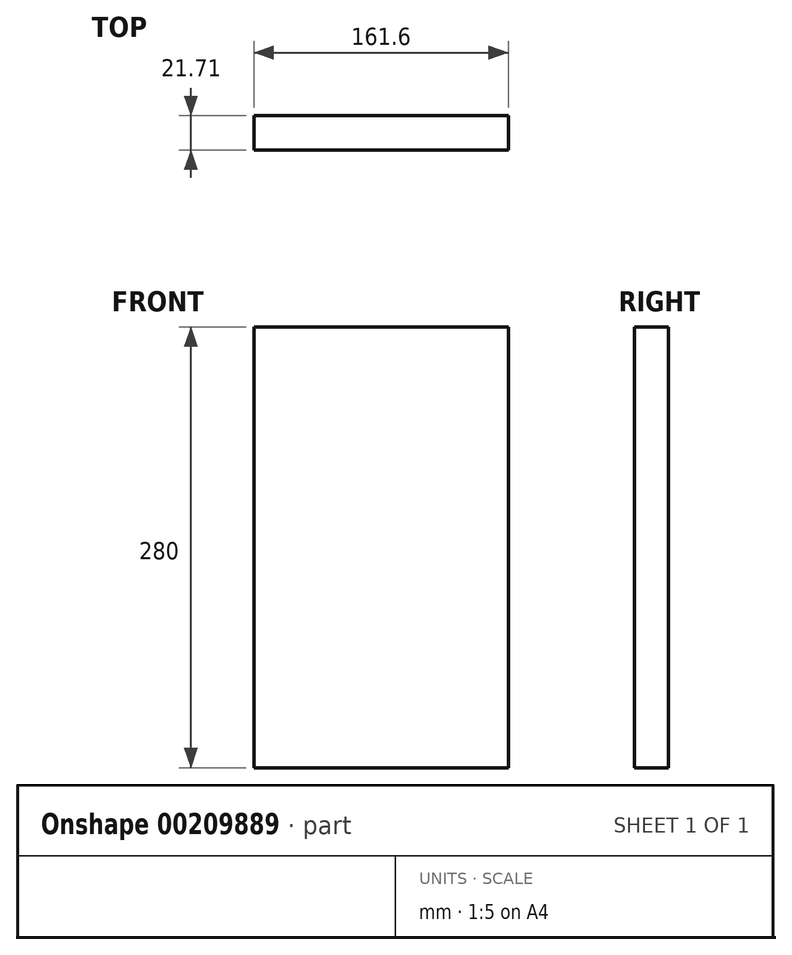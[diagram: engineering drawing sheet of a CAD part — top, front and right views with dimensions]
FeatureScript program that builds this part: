
annotation { "Feature Type Name" : "Feature", "Feature Type Description" : "" }
export const myFeature = defineFeature(function(context is Context, id is Id, definition is map)
    precondition{}
    {
        {
            var Q0;
            Q0=qCreatedBy(makeId("Top.planeOp"),FACE);
            var sketch = newSketch(context, id + "F0", { "sketchPlane" : qUnion([Q0])});
            skLineSegment(sketch, "E0.bottom", {"start": v(-97.37, 55.29) * mm, "end": v(64.23, 55.29) * mm});
            skLineSegment(sketch, "E0.top", {"start": v(-97.37, 33.58) * mm, "end": v(64.23, 33.58) * mm});
            skLineSegment(sketch, "E0.left", {"start": v(-97.37, 55.29) * mm, "end": v(-97.37, 33.58) * mm});
            skLineSegment(sketch, "E0.right", {"start": v(64.23, 55.29) * mm, "end": v(64.23, 33.58) * mm});
            skSolve(sketch);
        }
        {
            var Q0;
            Q0=makeQuery(id+"F0.imprint","IMPRINT",FACE,{"disambiguationData":[TD([[makeQuery(id+"F0.imprint","IMPRINT",EDGE,{"derivedFrom":sQuery(id+"F0.wireOp",EDGE,"E0.bottom")}),-1.0]])]});
            extrude(context, id + "F1", {"entities" : qUnion([Q0]), "depth" : 280 * mm});
        }
    });
